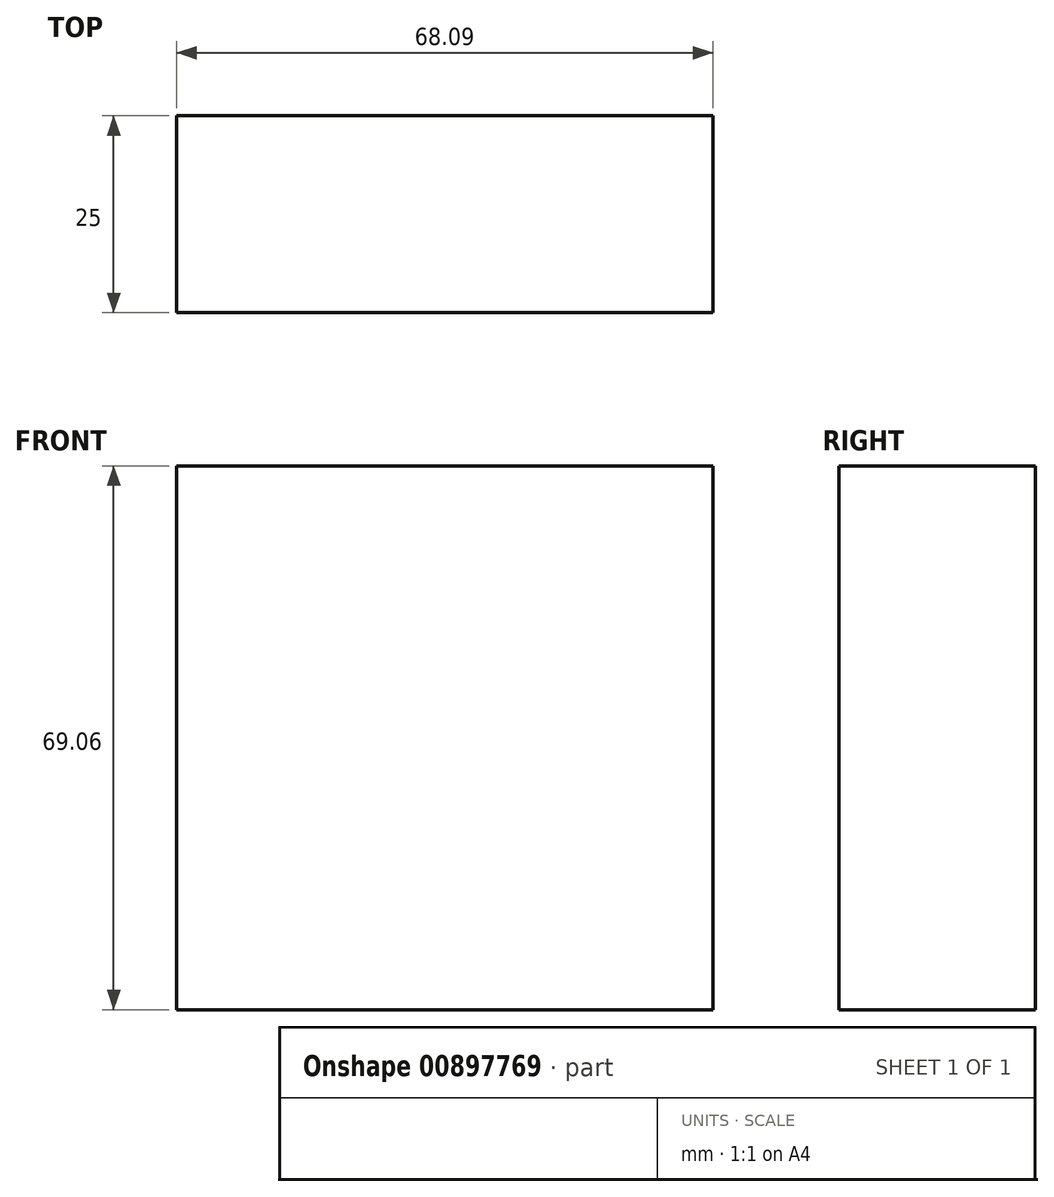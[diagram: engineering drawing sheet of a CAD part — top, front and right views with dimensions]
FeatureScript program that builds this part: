
annotation { "Feature Type Name" : "Feature", "Feature Type Description" : "" }
export const myFeature = defineFeature(function(context is Context, id is Id, definition is map)
    precondition{}
    {
        {
            var Q0;
            Q0=qCreatedBy(makeId("Front.planeOp"),FACE);
            var sketch = newSketch(context, id + "F0", { "sketchPlane" : qUnion([Q0])});
            skLineSegment(sketch, "E0.bottom", {"start": v(-161.72, -38.5) * mm, "end": v(-93.63, -38.5) * mm});
            skLineSegment(sketch, "E0.top", {"start": v(-161.72, 30.55) * mm, "end": v(-93.63, 30.55) * mm});
            skLineSegment(sketch, "E0.left", {"start": v(-161.72, -38.5) * mm, "end": v(-161.72, 30.55) * mm});
            skLineSegment(sketch, "E0.right", {"start": v(-93.63, -38.5) * mm, "end": v(-93.63, 30.55) * mm});
            skPoint(sketch, "E0.middle", {"position": v(-127.67, -3.98) * mm});
            skSolve(sketch);
        }
        {
            var Q0;
            Q0=makeQuery(id+"F0.imprint","IMPRINT",FACE,{"disambiguationData":[TD([[makeQuery(id+"F0.imprint","IMPRINT",EDGE,{"derivedFrom":sQuery(id+"F0.wireOp",EDGE,"E0.bottom")}),1.0]])]});
            var Q1;
            Q1=sQuery(id+"F0.wireOp",EDGE,"E0.left");
            var Q2;
            Q2=sQuery(id+"F0.wireOp",EDGE,"E0.bottom");
            var Q3;
            Q3=sQuery(id+"F0.wireOp",EDGE,"E0.right");
            var Q4;
            Q4=sQuery(id+"F0.wireOp",EDGE,"E0.top");
            extrude(context, id + "F1", {"entities" : qUnion([Q0]), "bodyType" : ToolBodyType.SURFACE, "surfaceEntities" : qUnion([Q1, Q2, Q3, Q4]), "depth" : 25 * mm, "offsetDistance" : 25 * mm});
        }
    });
